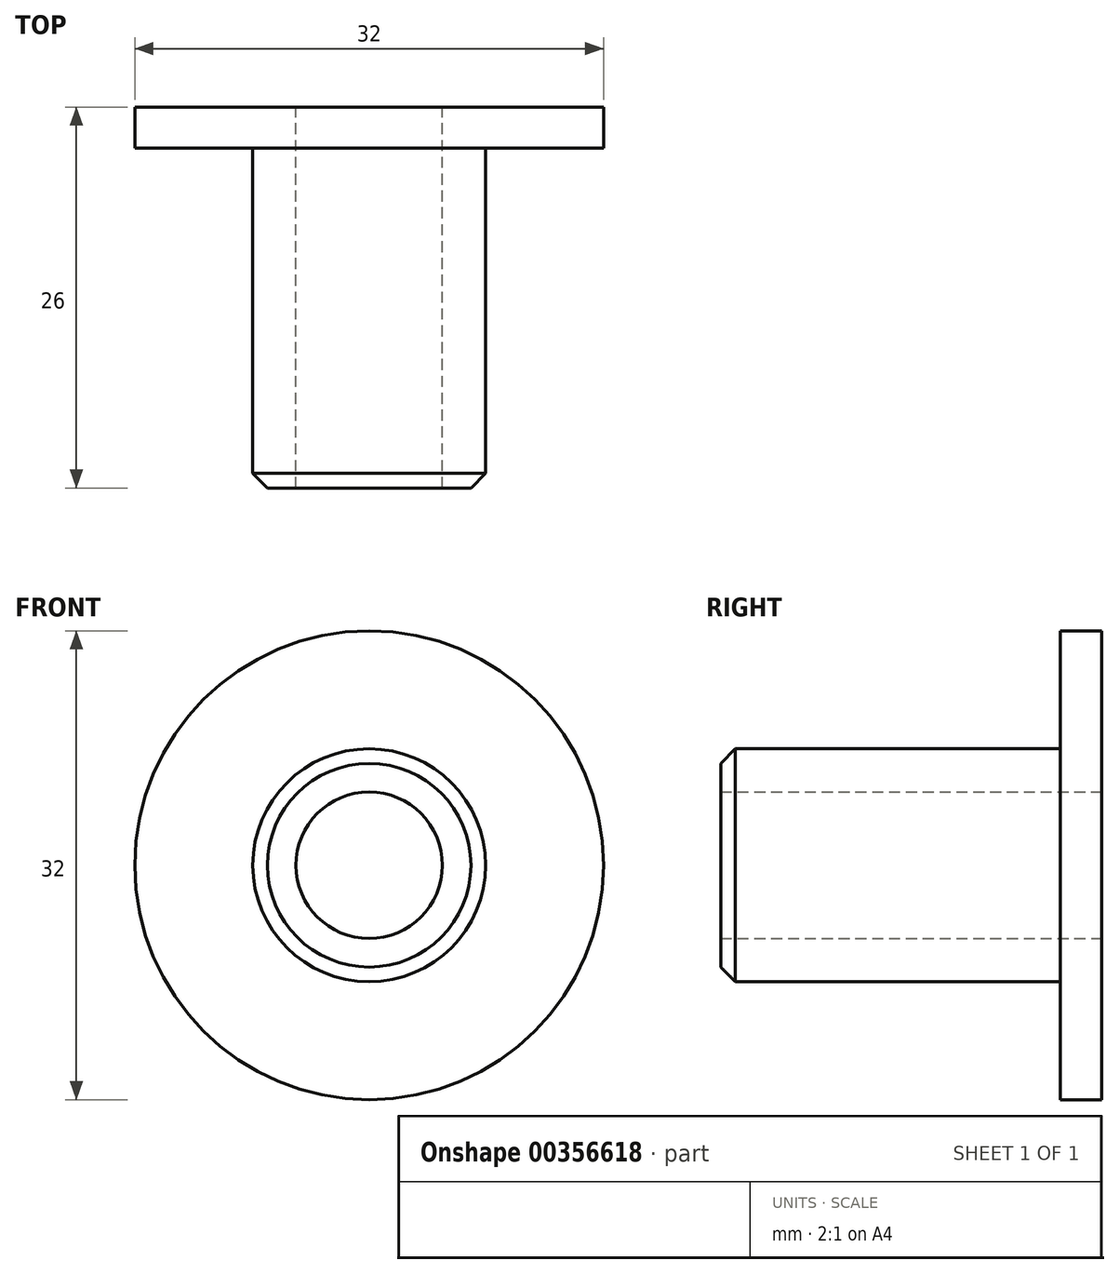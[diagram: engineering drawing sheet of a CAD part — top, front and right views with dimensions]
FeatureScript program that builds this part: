
annotation { "Feature Type Name" : "Feature", "Feature Type Description" : "" }
export const myFeature = defineFeature(function(context is Context, id is Id, definition is map)
    precondition{}
    {
        {
            var Q0;
            Q0=qCreatedBy(makeId("Front.planeOp"),FACE);
            var sketch = newSketch(context, id + "F0", { "sketchPlane" : qUnion([Q0])});
            skCircle(sketch, "E0", {"center": v(0, 0) * mm, "radius": 5 * mm});
            skCircle(sketch, "E1", {"center": v(0, 0) * mm, "radius": 7.95 * mm});
            skCircle(sketch, "E2", {"center": v(0, 0) * mm, "radius": 16 * mm});
            skSolve(sketch);
        }
        {
            var Q0;
            Q0=makeQuery(id+"F0.imprint","IMPRINT",FACE,{"disambiguationData":[TD([[makeQuery(id+"F0.imprint","IMPRINT",EDGE,{"derivedFrom":sQuery(id+"F0.wireOp",EDGE,"E0")}),-1.0]])]});
            extrude(context, id + "F1", {"entities" : qUnion([Q0]), "depth" : 26 * mm});
        }
        {
            var Q0;
            Q0=makeQuery(id+"F0.imprint","IMPRINT",FACE,{"disambiguationData":[TD([[makeQuery(id+"F0.imprint","IMPRINT",EDGE,{"derivedFrom":sQuery(id+"F0.wireOp",EDGE,"E1")}),-1.0]])]});
            extrude(context, id + "F2", {"entities" : qUnion([Q0]), "operationType" : NewBodyOperationType.ADD, "depth" : 2.81 * mm});
        }
        {
            var Q0;
            Q0=makeQuery(id+"F1.opExtrude","CAP_EDGE",EDGE,{"disambiguationData":[OSD([sQuery(id+"F0.wireOp",EDGE,"E1")])],"isStart":false});
            chamfer(context, id + "F3", {"entities" : qUnion([Q0]), "width" : 1 * mm, "tangentPropagation" : true});
        }
    });
